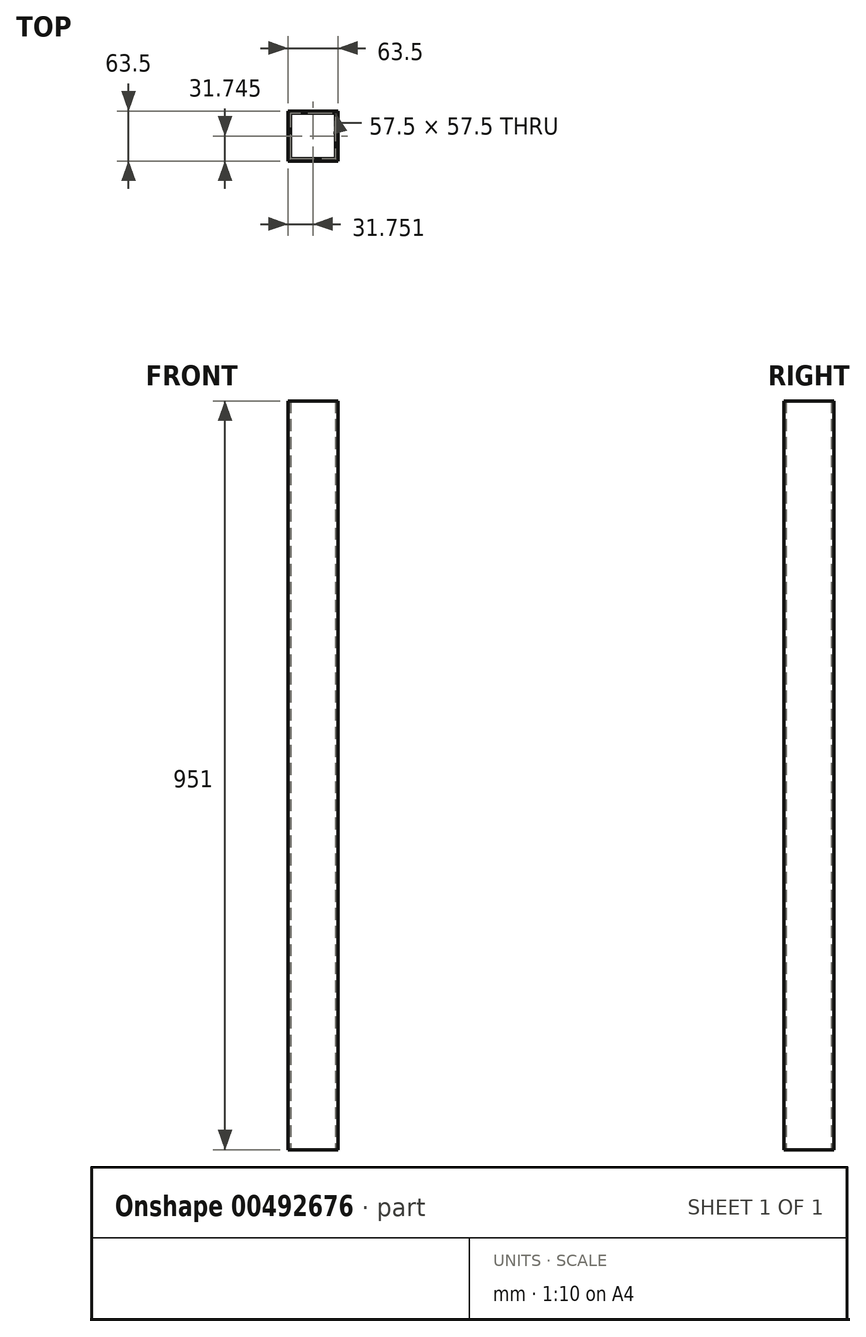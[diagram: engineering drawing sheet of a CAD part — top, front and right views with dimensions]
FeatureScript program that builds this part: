
annotation { "Feature Type Name" : "Feature", "Feature Type Description" : "" }
export const myFeature = defineFeature(function(context is Context, id is Id, definition is map)
    precondition{}
    {
        {
            var Q0;
            Q0=qCreatedBy(makeId("Top.planeOp"),FACE);
            var sketch = newSketch(context, id + "F0", { "sketchPlane" : qUnion([Q0])});
            skLineSegment(sketch, "E0.bottom", {"start": v(-18.8, 23) * mm, "end": v(38.7, 23) * mm});
            skLineSegment(sketch, "E0.top", {"start": v(-18.8, -34.5) * mm, "end": v(38.7, -34.5) * mm});
            skLineSegment(sketch, "E0.left", {"start": v(-18.8, 23) * mm, "end": v(-18.8, -34.5) * mm});
            skLineSegment(sketch, "E0.right", {"start": v(38.7, 23) * mm, "end": v(38.7, -34.5) * mm});
            skLineSegment(sketch, "E1.bottom", {"start": v(-21.8, 26) * mm, "end": v(41.7, 26) * mm});
            skLineSegment(sketch, "E1.top", {"start": v(-21.8, -37.5) * mm, "end": v(41.7, -37.5) * mm});
            skLineSegment(sketch, "E1.left", {"start": v(-21.8, 26) * mm, "end": v(-21.8, -37.5) * mm});
            skLineSegment(sketch, "E1.right", {"start": v(41.7, 26) * mm, "end": v(41.7, -37.5) * mm});
            skSolve(sketch);
        }
        {
            var Q0;
            Q0=qSketchRegion(id+"F0",true);
            extrude(context, id + "F1", {"entities" : qUnion([Q0]), "depth" : 951 * mm});
        }
    });
